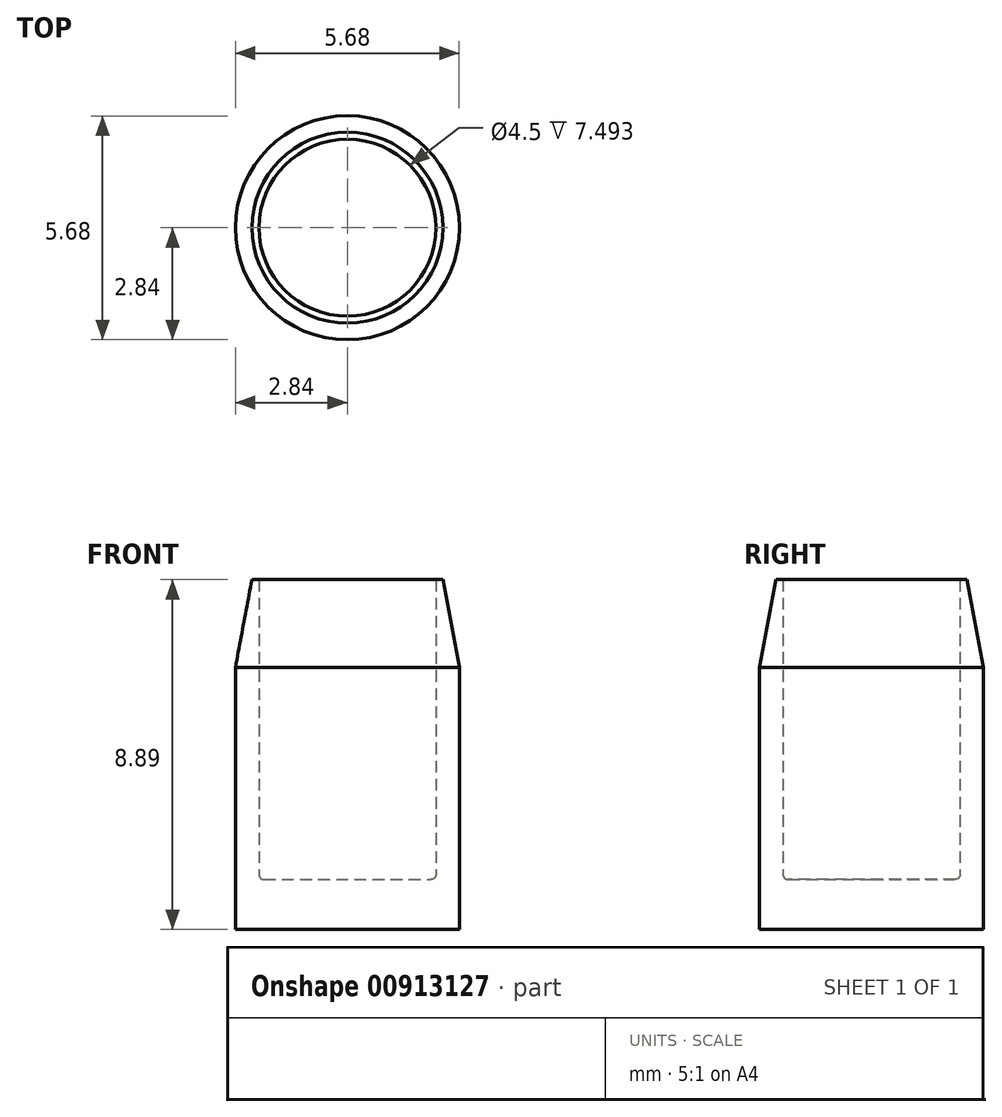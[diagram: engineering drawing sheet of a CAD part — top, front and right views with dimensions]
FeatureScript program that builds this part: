
annotation { "Feature Type Name" : "Feature", "Feature Type Description" : "" }
export const myFeature = defineFeature(function(context is Context, id is Id, definition is map)
    precondition{}
    {
        {
            var Q0;
            Q0=qCreatedBy(makeId("Front.planeOp"),FACE);
            var sketch = newSketch(context, id + "F0", { "sketchPlane" : qUnion([Q0])});
            skLineSegment(sketch, "E0", {"start": v(2.25, 8.9) * mm, "end": v(2.25, 1.4) * mm});
            skLineSegment(sketch, "E1", {"start": v(2.12, 1.27) * mm, "end": v(0, 1.27) * mm});
            skLineSegment(sketch, "E2.MirrorCS", {"start": v(-2.84, 6.66) * mm, "end": v(-2.25, 8.9) * mm, "construction": true});
            skLineSegment(sketch, "E3.MirrorCS", {"start": v(-2.84, 0) * mm, "end": v(-2.84, 6.66) * mm, "construction": true});
            skLineSegment(sketch, "E4.MirrorCS", {"start": v(-2.25, 8.9) * mm, "end": v(-2.25, 1.27) * mm, "construction": true});
            skLineSegment(sketch, "E5.MirrorCS", {"start": v(-2.25, 1.27) * mm, "end": v(0, 1.27) * mm, "construction": true});
            skLineSegment(sketch, "E6.MirrorCS", {"start": v(-2.84, 0) * mm, "end": v(0, 0) * mm, "construction": true});
            skLineSegment(sketch, "E7.MirrorCS", {"start": v(-2.25, 8.9) * mm, "end": v(-2.25, 1.27) * mm});
            skLineSegment(sketch, "E8", {"start": v(0, 1.69) * mm, "end": v(0, 13.44) * mm, "construction": true});
            skPoint(sketch, "E9.visualSharp", {"position": v(2.25, 1.27) * mm});
            skArc(sketch, "E9.filletArc", {"start": v(2.12, 1.27) * mm, "mid": v(2.21, 1.3) * mm, "end": v(2.25, 1.4) * mm});
            skPoint(sketch, "E10.orphan", {"position": v(2.84, 6.66) * mm});
            skPoint(sketch, "E11.orphan", {"position": v(0, 0) * mm});
            skArc(sketch, "E12", {"start": v(0, 0.4) * mm, "mid": v(-1.12, 0.3) * mm, "end": v(-2.2, 0) * mm, "construction": true});
            skLineSegment(sketch, "E13", {"start": v(0, 1.27) * mm, "end": v(0, 0) * mm});
            skLineSegment(sketch, "E14", {"start": v(2.84, 0) * mm, "end": v(0, 0) * mm});
            skLineSegment(sketch, "E15", {"start": v(2.25, 8.89) * mm, "end": v(2.43, 8.89) * mm});
            skLineSegment(sketch, "E16", {"start": v(2.84, 0) * mm, "end": v(2.84, 6.66) * mm});
            skLineSegment(sketch, "E17", {"start": v(2.84, 6.66) * mm, "end": v(2.43, 8.89) * mm});
            skSolve(sketch);
        }
        {
            var Q0;
            Q0=qSketchRegion(id+"F0",true);
            var Q1;
            Q1=sQuery(id+"F0.wireOp",EDGE,"E8");
            revolve(context, id + "F1", {"surfaceOperationType" : NewSurfaceOperationType.NEW, "entities" : qUnion([Q0]), "axis" : qUnion([Q1]), "revolveType" : RevolveType.FULL});
        }
    });
